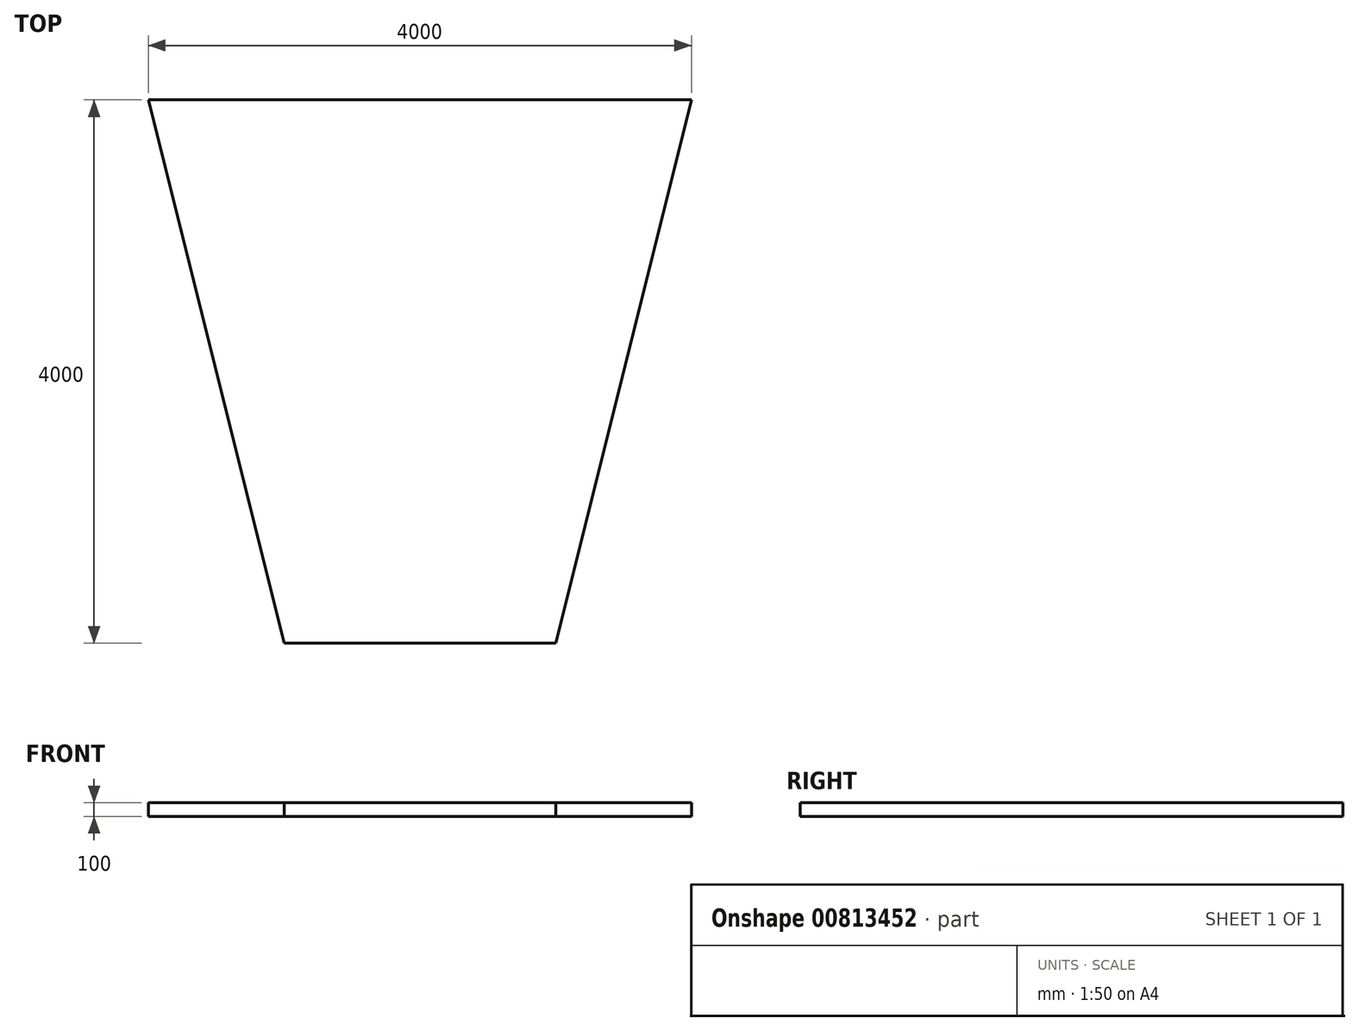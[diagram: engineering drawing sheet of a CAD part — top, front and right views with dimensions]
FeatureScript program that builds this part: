
annotation { "Feature Type Name" : "Feature", "Feature Type Description" : "" }
export const myFeature = defineFeature(function(context is Context, id is Id, definition is map)
    precondition{}
    {
        {
            var Q0;
            Q0=qCreatedBy(makeId("Top.planeOp"),FACE);
            var sketch = newSketch(context, id + "F0", { "sketchPlane" : qUnion([Q0])});
            skLineSegment(sketch, "E0", {"start": v(-1999.32, 1126.55) * mm, "end": v(2000.68, 1126.55) * mm});
            skLineSegment(sketch, "E1", {"start": v(2000.68, 1126.55) * mm, "end": v(1000.68, -2873.45) * mm});
            skLineSegment(sketch, "E2", {"start": v(1000.68, -2873.45) * mm, "end": v(-999.32, -2873.45) * mm});
            skLineSegment(sketch, "E3", {"start": v(-999.32, -2873.45) * mm, "end": v(-1999.32, 1126.55) * mm});
            skSolve(sketch);
        }
        {
            var Q0;
            Q0 = qSketchRegion(id + "F0", true);
            extrude(context, id + "F1", {"entities" : qUnion([Q0]), "depth" : 100 * mm, "offsetDistance" : 25 * mm});
        }
    });
